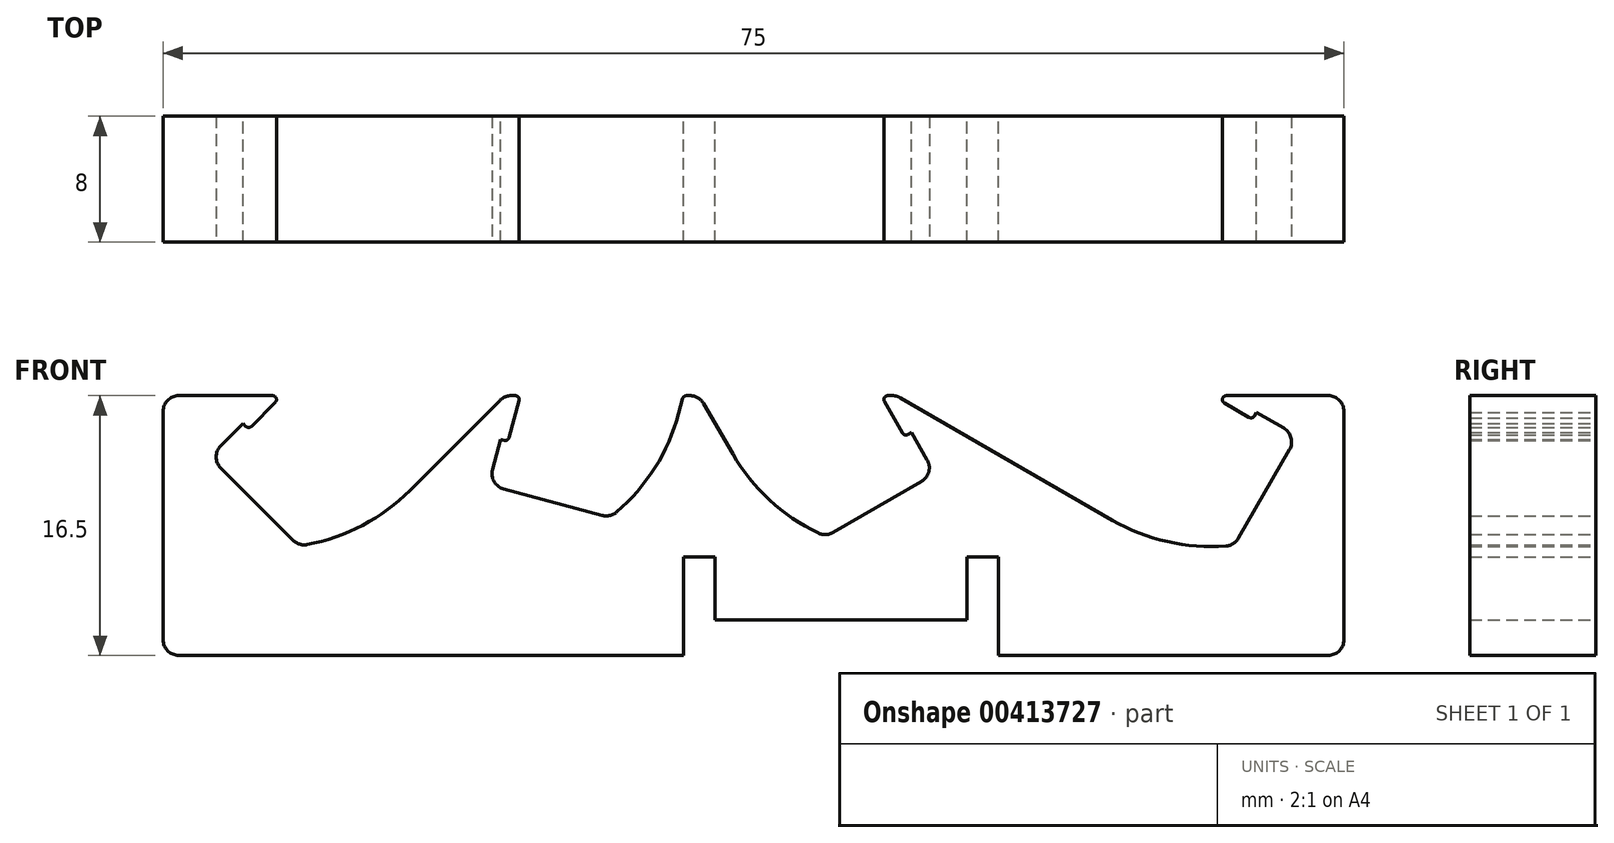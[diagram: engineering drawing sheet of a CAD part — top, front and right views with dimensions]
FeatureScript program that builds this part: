
annotation { "Feature Type Name" : "Feature", "Feature Type Description" : "" }
export const myFeature = defineFeature(function(context is Context, id is Id, definition is map)
    precondition{}
    {
        {
            assignVariable(context, id + "F0", {"name" : "width", "anyValue" : 8});
        }
        {
            var Q0;
            Q0=qCreatedBy(makeId("Front.planeOp"),FACE);
            var sketch = newSketch(context, id + "F1", { "sketchPlane" : qUnion([Q0])});
            skLineSegment(sketch, "E0", {"start": v(-37.5, 0) * mm, "end": v(-4.45, 0) * mm});
            skLineSegment(sketch, "E1", {"start": v(37.5, 0) * mm, "end": v(37.5, 16.5) * mm});
            skLineSegment(sketch, "E2", {"start": v(37.5, 16.5) * mm, "end": v(29.1, 16.5) * mm});
            skLineSegment(sketch, "E3", {"start": v(-37.5, 16.5) * mm, "end": v(-37.5, 0) * mm});
            skLineSegment(sketch, "E4", {"start": v(34.54, 13.93) * mm, "end": v(31.94, 15.43) * mm});
            skLineSegment(sketch, "E5", {"start": v(9.1, 16.5) * mm, "end": v(22.8, 8.58) * mm});
            skLineSegment(sketch, "E6", {"start": v(30.54, 7) * mm, "end": v(34.54, 13.93) * mm});
            skLineSegment(sketch, "E7", {"start": v(29.1, 16.5) * mm, "end": v(31.7, 15) * mm});
            skLineSegment(sketch, "E8", {"start": v(31.7, 15) * mm, "end": v(31.94, 15.43) * mm});
            skArc(sketch, "E9", {"start": v(22.8, 8.58) * mm, "mid": v(26.54, 7.16) * mm, "end": v(30.54, 7) * mm});
            skLineSegment(sketch, "E10", {"start": v(11.53, 11.55) * mm, "end": v(10.03, 14.15) * mm});
            skLineSegment(sketch, "E11", {"start": v(-3.45, 16.5) * mm, "end": v(-1.31, 12.8) * mm});
            skLineSegment(sketch, "E12", {"start": v(4.6, 7.55) * mm, "end": v(11.53, 11.55) * mm});
            skLineSegment(sketch, "E13", {"start": v(8.1, 16.5) * mm, "end": v(9.6, 13.9) * mm});
            skLineSegment(sketch, "E14", {"start": v(9.6, 13.9) * mm, "end": v(10.03, 14.15) * mm});
            skArc(sketch, "E15", {"start": v(-1.31, 12.8) * mm, "mid": v(1.22, 9.7) * mm, "end": v(4.6, 7.55) * mm});
            skLineSegment(sketch, "E16.MirrorCS", {"start": v(-34.54, 12.6) * mm, "end": v(-32.42, 14.73) * mm});
            skLineSegment(sketch, "E17.MirrorCS", {"start": v(-32.07, 14.37) * mm, "end": v(-32.42, 14.73) * mm});
            skLineSegment(sketch, "E18.MirrorCS", {"start": v(-29.95, 16.5) * mm, "end": v(-32.07, 14.37) * mm});
            skArc(sketch, "E19.MirrorCS", {"start": v(-21.81, 10.48) * mm, "mid": v(-25.06, 8.14) * mm, "end": v(-28.89, 6.95) * mm});
            skLineSegment(sketch, "E20.MirrorCS", {"start": v(-28.89, 6.95) * mm, "end": v(-34.54, 12.6) * mm});
            skLineSegment(sketch, "E21.MirrorCS", {"start": v(-15.8, 16.5) * mm, "end": v(-21.81, 10.48) * mm});
            skLineSegment(sketch, "E22", {"start": v(-37.5, 16.5) * mm, "end": v(-29.95, 16.5) * mm});
            skLineSegment(sketch, "E23", {"start": v(8.1, 16.5) * mm, "end": v(9.1, 16.5) * mm});
            skLineSegment(sketch, "E24.MirrorCS", {"start": v(-15.58, 13.6) * mm, "end": v(-16.06, 13.73) * mm});
            skArc(sketch, "E25.MirrorCS", {"start": v(-4.76, 15.36) * mm, "mid": v(-6.4, 11.7) * mm, "end": v(-9.11, 8.76) * mm});
            skLineSegment(sketch, "E26.MirrorCS", {"start": v(-14.8, 16.5) * mm, "end": v(-15.58, 13.6) * mm});
            skLineSegment(sketch, "E27.MirrorCS", {"start": v(-4.45, 16.5) * mm, "end": v(-4.76, 15.36) * mm});
            skLineSegment(sketch, "E28.MirrorCS", {"start": v(-16.84, 10.83) * mm, "end": v(-16.06, 13.73) * mm});
            skLineSegment(sketch, "E29.MirrorCS", {"start": v(-9.11, 8.76) * mm, "end": v(-16.84, 10.83) * mm});
            skLineSegment(sketch, "E30", {"start": v(-4.45, 16.5) * mm, "end": v(-3.45, 16.5) * mm});
            skLineSegment(sketch, "E31", {"start": v(-15.8, 16.5) * mm, "end": v(-14.8, 16.5) * mm});
            skLineSegment(sketch, "E32", {"start": v(13.55, 2.25) * mm, "end": v(13.55, 6.25) * mm});
            skLineSegment(sketch, "E33", {"start": v(13.55, 6.25) * mm, "end": v(15.55, 6.25) * mm});
            skLineSegment(sketch, "E34", {"start": v(15.55, 6.25) * mm, "end": v(15.55, 0) * mm});
            skLineSegment(sketch, "E35.trimOffspring", {"start": v(15.55, 0) * mm, "end": v(37.5, 0) * mm});
            skLineSegment(sketch, "E36", {"start": v(0, -4.45) * mm, "end": v(0, 21.54) * mm, "construction": true});
            skLineSegment(sketch, "E37.MirrorCS", {"start": v(-2.45, 2.25) * mm, "end": v(-2.45, 6.25) * mm});
            skLineSegment(sketch, "E38.MirrorCS", {"start": v(-2.45, 6.25) * mm, "end": v(-4.45, 6.25) * mm});
            skLineSegment(sketch, "E39.MirrorCS", {"start": v(-4.45, 6.25) * mm, "end": v(-4.45, 0) * mm});
            skLineSegment(sketch, "E40", {"start": v(-34.54, 14.88) * mm, "end": v(-34.54, 10.13) * mm, "construction": true});
            skLineSegment(sketch, "E41", {"start": v(34.54, 15.63) * mm, "end": v(34.54, 11.44) * mm, "construction": true});
            skLineSegment(sketch, "E42", {"start": v(-2.45, 2.25) * mm, "end": v(13.55, 2.25) * mm});
            skSolve(sketch);
        }
        {
            var Q0;
            Q0 = qSketchRegion(id + "F1", true);
            extrude(context, id + "F2", {"entities" : qUnion([Q0]), "depth" : (getVariable(context, 'width')) * mm, "symmetric" : true});
        }
        {
            var Q0;
            Q0=makeQuery(id+"F2.opExtrude","SWEPT_EDGE",EDGE,{"disambiguationData":[OSD([sQuery(id+"F1.wireOp",EDGE,"E0"),sQuery(id+"F1.wireOp",EDGE,"E3")])]});
            var Q1;
            Q1=makeQuery(id+"F2.opExtrude","SWEPT_EDGE",EDGE,{"disambiguationData":[OSD([sQuery(id+"F1.wireOp",EDGE,"E1"),sQuery(id+"F1.wireOp",EDGE,"E35.trimOffspring")])]});
            var Q2;
            Q2=makeQuery(id+"F2.opExtrude","SWEPT_EDGE",EDGE,{"disambiguationData":[OSD([sQuery(id+"F1.wireOp",EDGE,"E1"),sQuery(id+"F1.wireOp",EDGE,"E2")])]});
            var Q3;
            Q3=makeQuery(id+"F2.opExtrude","SWEPT_EDGE",EDGE,{"disambiguationData":[OSD([sQuery(id+"F1.wireOp",EDGE,"E5"),sQuery(id+"F1.wireOp",EDGE,"E23")])]});
            var Q4;
            Q4=makeQuery(id+"F2.opExtrude","SWEPT_EDGE",EDGE,{"disambiguationData":[OSD([sQuery(id+"F1.wireOp",EDGE,"E6"),sQuery(id+"F1.wireOp",EDGE,"E9")])]});
            var Q5;
            Q5=makeQuery(id+"F2.opExtrude","SWEPT_EDGE",EDGE,{"disambiguationData":[OSD([sQuery(id+"F1.wireOp",EDGE,"E1"),sQuery(id+"F1.wireOp",EDGE,"E2")])]});
            var Q6;
            Q6=makeQuery(id+"F2.opExtrude","SWEPT_EDGE",EDGE,{"disambiguationData":[OSD([sQuery(id+"F1.wireOp",EDGE,"E12"),sQuery(id+"F1.wireOp",EDGE,"E15")])]});
            var Q7;
            Q7=makeQuery(id+"F2.opExtrude","SWEPT_EDGE",EDGE,{"disambiguationData":[OSD([sQuery(id+"F1.wireOp",EDGE,"E4"),sQuery(id+"F1.wireOp",EDGE,"E6")])]});
            var Q8;
            Q8=makeQuery(id+"F2.opExtrude","SWEPT_EDGE",EDGE,{"disambiguationData":[OSD([sQuery(id+"F1.wireOp",EDGE,"E25.MirrorCS"),sQuery(id+"F1.wireOp",EDGE,"E29.MirrorCS")])]});
            var Q9;
            Q9=makeQuery(id+"F2.opExtrude","SWEPT_EDGE",EDGE,{"disambiguationData":[OSD([sQuery(id+"F1.wireOp",EDGE,"E19.MirrorCS"),sQuery(id+"F1.wireOp",EDGE,"E20.MirrorCS")])]});
            var Q10;
            Q10=makeQuery(id+"F2.opExtrude","SWEPT_EDGE",EDGE,{"disambiguationData":[OSD([sQuery(id+"F1.wireOp",EDGE,"E11"),sQuery(id+"F1.wireOp",EDGE,"E30")])]});
            var Q11;
            Q11=makeQuery(id+"F2.opExtrude","SWEPT_EDGE",EDGE,{"disambiguationData":[OSD([sQuery(id+"F1.wireOp",EDGE,"E11"),sQuery(id+"F1.wireOp",EDGE,"E15")])]});
            var Q12;
            Q12=makeQuery(id+"F2.opExtrude","SWEPT_EDGE",EDGE,{"disambiguationData":[OSD([sQuery(id+"F1.wireOp",EDGE,"E21.MirrorCS"),sQuery(id+"F1.wireOp",EDGE,"E31")])]});
            var Q13;
            Q13=makeQuery(id+"F2.opExtrude","SWEPT_EDGE",EDGE,{"disambiguationData":[OSD([sQuery(id+"F1.wireOp",EDGE,"E3"),sQuery(id+"F1.wireOp",EDGE,"E22")])]});
            var Q14;
            Q14=makeQuery(id+"F2.opExtrude","SWEPT_EDGE",EDGE,{"disambiguationData":[OSD([sQuery(id+"F1.wireOp",EDGE,"E0"),sQuery(id+"F1.wireOp",EDGE,"E3")])]});
            var Q15;
            Q15=makeQuery(id+"F2.opExtrude","SWEPT_EDGE",EDGE,{"disambiguationData":[OSD([sQuery(id+"F1.wireOp",EDGE,"E10"),sQuery(id+"F1.wireOp",EDGE,"E12")])]});
            var Q16;
            Q16=makeQuery(id+"F2.opExtrude","SWEPT_EDGE",EDGE,{"disambiguationData":[OSD([sQuery(id+"F1.wireOp",EDGE,"E28.MirrorCS"),sQuery(id+"F1.wireOp",EDGE,"E29.MirrorCS")])]});
            var Q17;
            Q17=makeQuery(id+"F2.opExtrude","SWEPT_EDGE",EDGE,{"disambiguationData":[OSD([sQuery(id+"F1.wireOp",EDGE,"E16.MirrorCS"),sQuery(id+"F1.wireOp",EDGE,"E20.MirrorCS")])]});
            fillet(context, id + "F3", {"entities" : qUnion([Q0, Q1, Q2, Q3, Q4, Q5, Q6, Q7, Q8, Q9, Q10, Q11, Q12, Q13, Q14, Q15, Q16, Q17]), "radius" : 1 * mm, "tangentPropagation" : true, "allowEdgeOverflow" : false});
        }
        {
            var Q0;
            Q0=makeQuery(id+"F2.opExtrude","SWEPT_EDGE",EDGE,{"disambiguationData":[OSD([sQuery(id+"F1.wireOp",EDGE,"767bfe6d-25ba-4c75-bf21-9cad5bb40aba.trimOffspring"),sQuery(id+"F1.wireOp",EDGE,"E13")])]});
            var Q1;
            Q1=makeQuery(id+"F2.opExtrude","SWEPT_EDGE",EDGE,{"disambiguationData":[OSD([sQuery(id+"F1.wireOp",EDGE,"E2"),sQuery(id+"F1.wireOp",EDGE,"E7")])]});
            var Q2;
            Q2=makeQuery(id+"F2.opExtrude","SWEPT_EDGE",EDGE,{"disambiguationData":[OSD([sQuery(id+"F1.wireOp",EDGE,"560a6a0f-7ae7-4148-8214-601ab04e107c"),sQuery(id+"F1.wireOp",EDGE,"YHAuL3Ue-cdt5-6urX-E68J-8J9TxOycDoPi")])]});
            var Q3;
            Q3=makeQuery(id+"F2.opExtrude","SWEPT_EDGE",EDGE,{"disambiguationData":[OSD([sQuery(id+"F1.wireOp",EDGE,"E27.MirrorCS"),sQuery(id+"F1.wireOp",EDGE,"E30")])]});
            var Q4;
            Q4=makeQuery(id+"F2.opExtrude","SWEPT_EDGE",EDGE,{"disambiguationData":[OSD([sQuery(id+"F1.wireOp",EDGE,"12972354-9dc3-415d-ba0d-aa30431c763b"),sQuery(id+"F1.wireOp",EDGE,"E30")])]});
            var Q5;
            Q5=makeQuery(id+"F2.opExtrude","SWEPT_EDGE",EDGE,{"disambiguationData":[OSD([sQuery(id+"F1.wireOp",EDGE,"E26.MirrorCS"),sQuery(id+"F1.wireOp",EDGE,"E31")])]});
            var Q6;
            Q6=makeQuery(id+"F2.opExtrude","SWEPT_EDGE",EDGE,{"disambiguationData":[OSD([sQuery(id+"F1.wireOp",EDGE,"E18.MirrorCS"),sQuery(id+"F1.wireOp",EDGE,"E22")])]});
            var Q7;
            Q7=makeQuery(id+"F2.opExtrude","SWEPT_EDGE",EDGE,{"disambiguationData":[OSD([sQuery(id+"F1.wireOp",EDGE,"E7"),sQuery(id+"F1.wireOp",EDGE,"E8")])]});
            var Q8;
            Q8=makeQuery(id+"F2.opExtrude","SWEPT_EDGE",EDGE,{"disambiguationData":[OSD([sQuery(id+"F1.wireOp",EDGE,"560a6a0f-7ae7-4148-8214-601ab04e107c"),sQuery(id+"F1.wireOp",EDGE,"371f2087-f31c-4a49-acf1-9fe8cb99871e")])]});
            var Q9;
            Q9=makeQuery(id+"F2.opExtrude","SWEPT_EDGE",EDGE,{"disambiguationData":[OSD([sQuery(id+"F1.wireOp",EDGE,"E24.MirrorCS"),sQuery(id+"F1.wireOp",EDGE,"E26.MirrorCS")])]});
            var Q10;
            Q10=makeQuery(id+"F2.opExtrude","SWEPT_EDGE",EDGE,{"disambiguationData":[OSD([sQuery(id+"F1.wireOp",EDGE,"E17.MirrorCS"),sQuery(id+"F1.wireOp",EDGE,"E18.MirrorCS")])]});
            fillet(context, id + "F4", {"entities" : qUnion([Q0, Q1, Q2, Q3, Q4, Q5, Q6, Q7, Q8, Q9, Q10]), "radius" : 0.25 * mm, "tangentPropagation" : true, "allowEdgeOverflow" : false});
        }
    });
